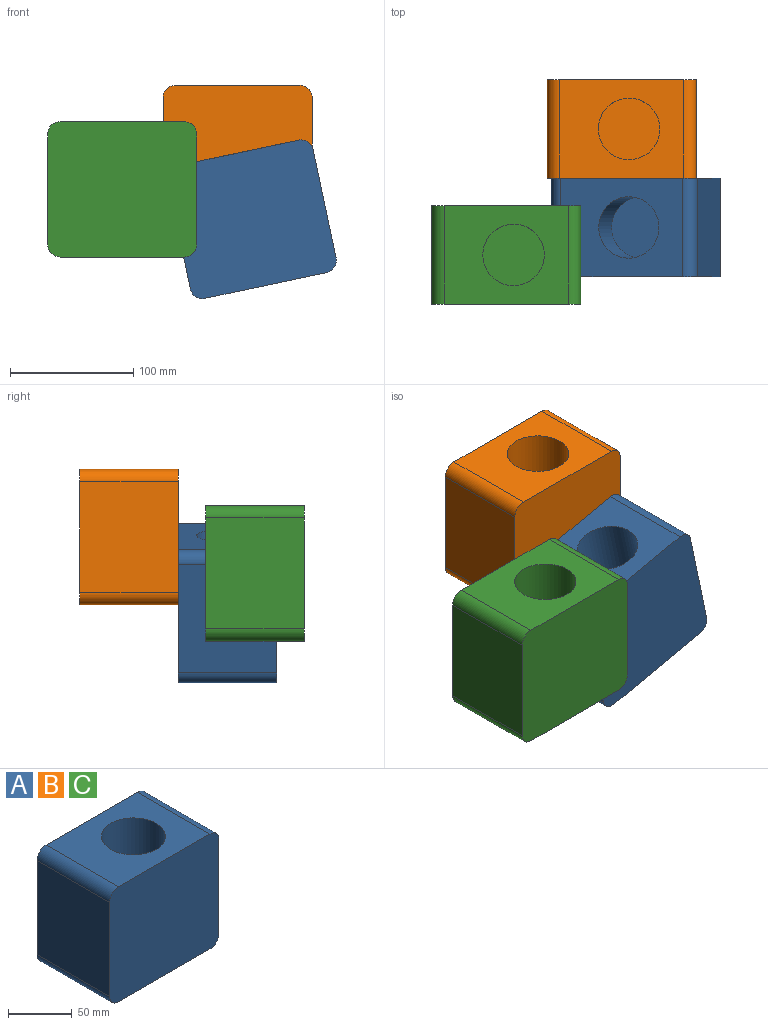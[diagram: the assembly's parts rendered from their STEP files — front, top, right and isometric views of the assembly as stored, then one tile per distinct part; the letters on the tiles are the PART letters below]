
ASSEMBLY  parts=3 mates=1
PART A: 12 faces, bbox 121x80x110 mm
  f0: plane 101.04x80mm, normal (0,0,1), area 6119.6mm2, adj f4,f5,f6,f9,f10
  f1: plane 90.01x80mm, normal (-1,0,0), area 7200.6mm2, adj f4,f5,f6,f7
  f2: plane 101.04x80mm, normal (0,0,-1), area 8083.1mm2, adj f4,f5,f7,f8
  f3: plane 90.01x80mm, normal (1,0,0), area 7200.6mm2, adj f4,f5,f8,f9
  f4: plane 121.04x110.01mm, normal (0,-1,0), area 13229.3mm2, adj f0,f1,f2,f3,f6,f7,f8,f9
  f5: plane 121.04x110.01mm, normal (0,1,0), area 13229.3mm2, adj f0,f1,f2,f3,f6,f7,f8,f9
  f6: cylinder r=10mm len=80mm, axis (0,-1,0), area 1256.6mm2, adj f0,f1,f4,f5
  f7: cylinder r=10mm len=80mm, axis (0,1,0), area 1256.6mm2, adj f1,f2,f4,f5
  f8: cylinder r=10mm len=80mm, axis (0,-1,0), area 1256.6mm2, adj f2,f3,f4,f5
  f9: cylinder r=10mm len=80mm, axis (0,1,0), area 1256.6mm2, adj f0,f3,f4,f5
  f10: cylinder r=25mm len=50mm, axis (0,0,1), area 7854mm2, adj f0,f11
  f11: plane 50x50mm, normal (0,0,1), area 1963.5mm2, adj f10
PART B: same geometry as A
PART C: same geometry as A
PLACE A rot(axis=(0,-1,0),12deg) t=(-31.6,-80,-105.4)mm
PLACE B t=(-42.97,0,-52.84)mm
PLACE C t=(-136.81,-102.34,-82.34)mm
MATE revolute A.f5 <-> B.f4  axis (0,1,0) through (-48.96,-80,-52.38)mm
